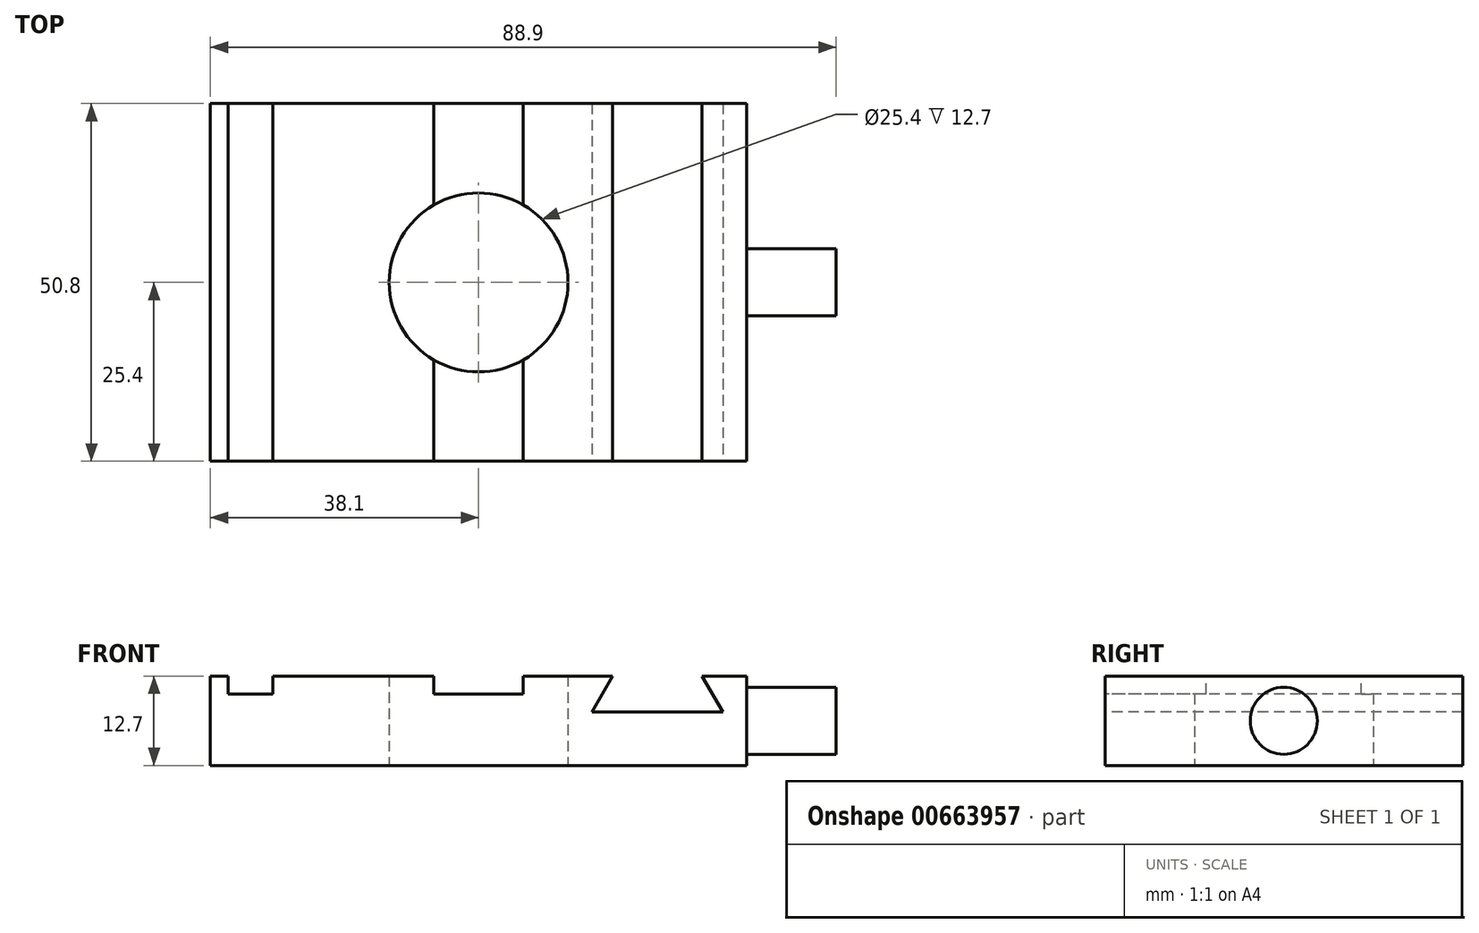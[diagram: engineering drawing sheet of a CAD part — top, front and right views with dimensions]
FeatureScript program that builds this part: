
annotation { "Feature Type Name" : "Feature", "Feature Type Description" : "" }
export const myFeature = defineFeature(function(context is Context, id is Id, definition is map)
    precondition{}
    {
        {
            var Q0;
            Q0=qCreatedBy(makeId("Top.planeOp"),FACE);
            var sketch = newSketch(context, id + "F0", { "sketchPlane" : qUnion([Q0])});
            skLineSegment(sketch, "E0.bottom", {"start": v(38.1, 25.4) * mm, "end": v(-38.1, 25.4) * mm});
            skLineSegment(sketch, "E0.top", {"start": v(38.1, -25.4) * mm, "end": v(-38.1, -25.4) * mm});
            skLineSegment(sketch, "E0.left", {"start": v(38.1, 25.4) * mm, "end": v(38.1, -25.4) * mm});
            skLineSegment(sketch, "E0.right", {"start": v(-38.1, 25.4) * mm, "end": v(-38.1, -25.4) * mm});
            skPoint(sketch, "E0.middle", {"position": v(0, 0) * mm});
            skCircle(sketch, "E1", {"center": v(0, 0) * mm, "radius": 12.7 * mm});
            skSolve(sketch);
        }
        {
            var Q0;
            Q0=makeQuery(id+"F0.imprint","IMPRINT",FACE,{"disambiguationData":[TD([[makeQuery(id+"F0.imprint","IMPRINT",EDGE,{"derivedFrom":sQuery(id+"F0.wireOp",EDGE,"E0.bottom")}),1.0]])]});
            extrude(context, id + "F1", {"entities" : qUnion([Q0]), "depth" : 12.7 * mm, "offsetDistance" : 25.4 * mm});
        }
        {
            var Q0;
            Q0=makeQuery(id+"F1.opExtrude","CAP_FACE",FACE,{"disambiguationData":[OSD([sQuery(id+"F0.wireOp",EDGE,"E0.bottom"),sQuery(id+"F0.wireOp",EDGE,"E0.top"),sQuery(id+"F0.wireOp",EDGE,"E0.left"),sQuery(id+"F0.wireOp",EDGE,"E0.right"),sQuery(id+"F0.wireOp",EDGE,"E1")])],"isStart":false});
            var sketch = newSketch(context, id + "F2", { "sketchPlane" : qUnion([Q0])});
            skLineSegment(sketch, "E2.bottom", {"start": v(-35.56, 25.4) * mm, "end": v(-29.21, 25.4) * mm});
            skLineSegment(sketch, "E2.top", {"start": v(-35.56, -25.4) * mm, "end": v(-29.21, -25.4) * mm});
            skLineSegment(sketch, "E2.left", {"start": v(-35.56, 25.4) * mm, "end": v(-35.56, -25.4) * mm});
            skLineSegment(sketch, "E2.right", {"start": v(-29.21, 25.4) * mm, "end": v(-29.21, -25.4) * mm});
            skLineSegment(sketch, "E3", {"start": v(-6.35, 25.4) * mm, "end": v(-6.35, -25.4) * mm});
            skLineSegment(sketch, "E4", {"start": v(-6.35, -25.4) * mm, "end": v(6.35, -25.4) * mm});
            skLineSegment(sketch, "E5", {"start": v(6.35, -25.4) * mm, "end": v(6.35, 25.4) * mm});
            skPoint(sketch, "E6", {"position": v(0, 0) * mm});
            skLineSegment(sketch, "E7", {"start": v(-6.35, 25.4) * mm, "end": v(6.35, 25.4) * mm, "construction": true});
            skLineSegment(sketch, "E8", {"start": v(0, 25.4) * mm, "end": v(0, -25.4) * mm, "construction": true});
            skSolve(sketch);
        }
        {
            var Q0;
            Q0=makeQuery(id+"F2.imprint","IMPRINT",FACE,{"disambiguationData":[TD([[makeQuery(id+"F2.imprint","IMPRINT",EDGE,{"derivedFrom":sQuery(id+"F2.wireOp",EDGE,"E2.bottom")}),1.0]])]});
            var Q1;
            {var subQ0=sQuery(id+"F2.wireOp",EDGE,"E4");Q1=makeQuery(id+"F2.imprint","IMPRINT",FACE,{"disambiguationData":[TD([[makeQuery(id+"F2.imprint","IMPRINT",EDGE,{"derivedFrom":subQ0}),-1.0]])]});}
            var Q2;
            {var subQ0=sQuery(id+"F2.wireOp",EDGE,"E3");var subQ1=makeQuery(id+"F1.opExtrude","CAP_EDGE",EDGE,{"disambiguationData":[OSD([sQuery(id+"F0.wireOp",EDGE,"E0.bottom")])],"isStart":false});var subQ2=makeQuery(id+"F2.imprint","INTERSECT",VERTEX,{"derivedFrom":[subQ1,subQ0]});Q2=makeQuery(id+"F2.imprint","IMPRINT",FACE,{"disambiguationData":[TD([[makeQuery(id+"F2.imprint","IMPRINT",EDGE,{"disambiguationData":[TD([[subQ2,-1.0]])],"derivedFrom":subQ0}),1.0]])]});}
            extrude(context, id + "F3", {"entities" : qUnion([Q0, Q1, Q2]), "operationType" : NewBodyOperationType.REMOVE, "oppositeDirection" : true, "depth" : 2.54 * mm, "offsetDistance" : 25.4 * mm});
        }
        {
            var Q0;
            Q0=makeQuery(id+"F1.opExtrude","SWEPT_FACE",FACE,{"disambiguationData":[OSD([sQuery(id+"F0.wireOp",EDGE,"E0.top")])]});
            var sketch = newSketch(context, id + "F4", { "sketchPlane" : qUnion([Q0])});
            skLineSegment(sketch, "E9", {"start": v(19.05, 12.7) * mm, "end": v(16.12, 7.62) * mm});
            skLineSegment(sketch, "E10", {"start": v(16.12, 7.62) * mm, "end": v(34.68, 7.62) * mm});
            skLineSegment(sketch, "E11", {"start": v(34.68, 7.62) * mm, "end": v(31.75, 12.7) * mm});
            skLineSegment(sketch, "E12", {"start": v(31.75, 12.7) * mm, "end": v(19.05, 12.7) * mm});
            skLineSegment(sketch, "E13", {"start": v(25.4, 7.62) * mm, "end": v(25.4, 12.7) * mm, "construction": true});
            skSolve(sketch);
        }
        {
            var Q0;
            Q0=makeQuery(id+"F4.imprint","IMPRINT",FACE,{"disambiguationData":[TD([[makeQuery(id+"F4.imprint","IMPRINT",EDGE,{"derivedFrom":sQuery(id+"F4.wireOp",EDGE,"E9")}),1.0]])]});
            extrude(context, id + "F5", {"entities" : qUnion([Q0]), "operationType" : NewBodyOperationType.REMOVE, "endBound" : BoundingType.THROUGH_ALL, "oppositeDirection" : true, "depth" : 25.4 * mm, "offsetDistance" : 25.4 * mm});
        }
        {
            var Q0;
            Q0=makeQuery(id+"F1.opExtrude","SWEPT_FACE",FACE,{"disambiguationData":[OSD([sQuery(id+"F0.wireOp",EDGE,"E0.left")])]});
            var sketch = newSketch(context, id + "F6", { "sketchPlane" : qUnion([Q0])});
            skCircle(sketch, "E14", {"center": v(0, 6.35) * mm, "radius": 4.76 * mm});
            skPoint(sketch, "E14.centerSnap0", {"position": v(-25.4, 6.35) * mm});
            skPoint(sketch, "E14.centerSnap1", {"position": v(0, 12.7) * mm});
            skSolve(sketch);
        }
        {
            var Q0;
            Q0=makeQuery(id+"F6.imprint","IMPRINT",FACE,{"disambiguationData":[TD([[makeQuery(id+"F6.imprint","IMPRINT",EDGE,{"derivedFrom":sQuery(id+"F6.wireOp",EDGE,"E14")}),1.0]])]});
            extrude(context, id + "F7", {"entities" : qUnion([Q0]), "operationType" : NewBodyOperationType.ADD, "depth" : 12.7 * mm, "offsetDistance" : 25.4 * mm});
        }
    });
